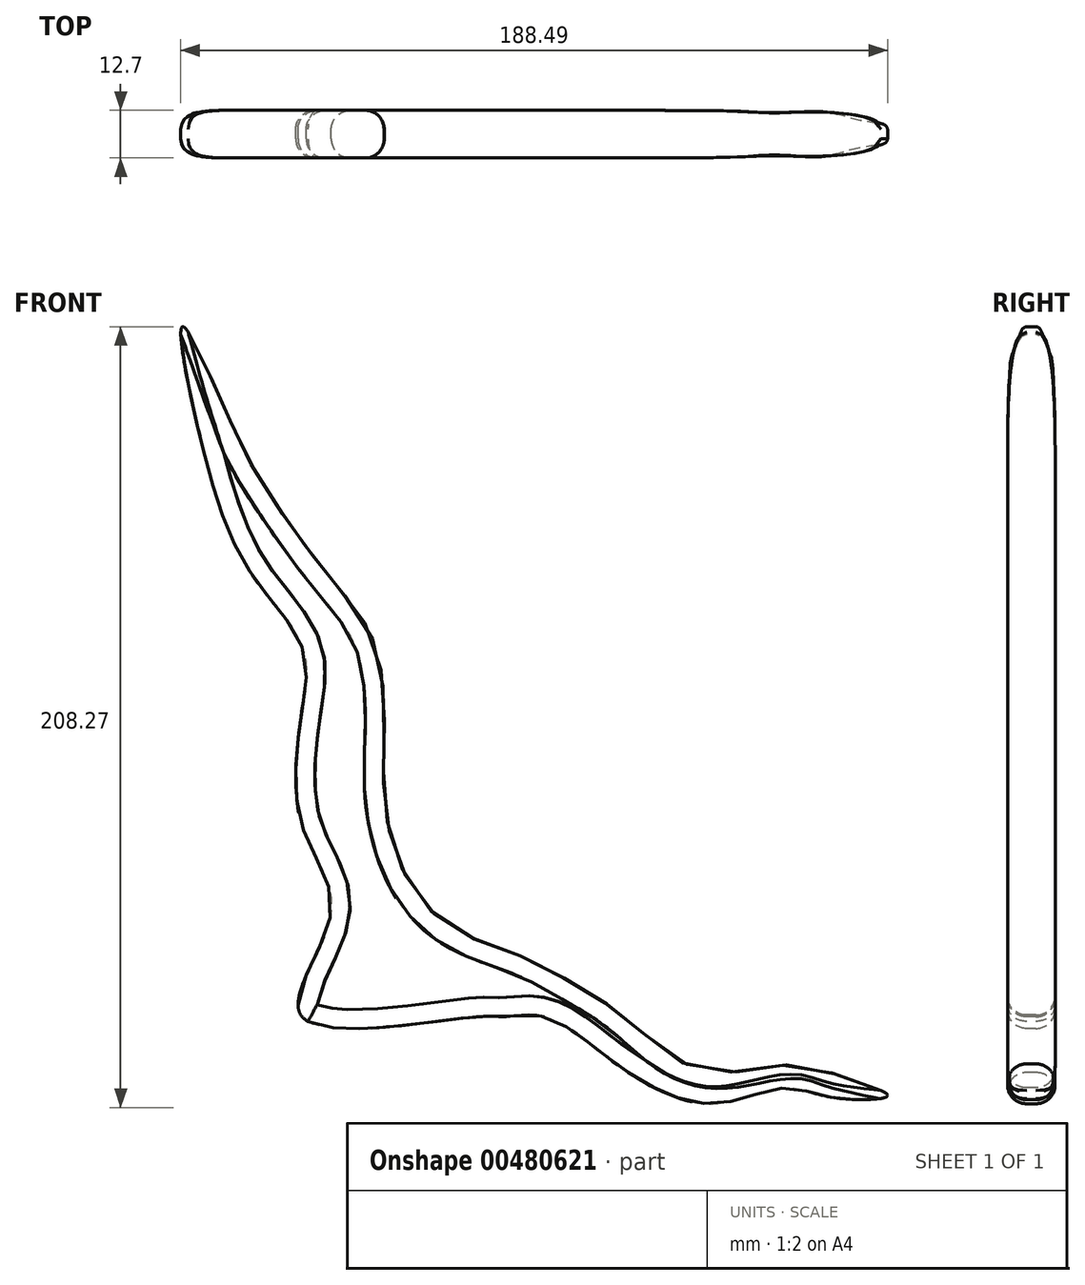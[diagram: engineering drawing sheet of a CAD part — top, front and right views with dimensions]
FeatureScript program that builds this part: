
annotation { "Feature Type Name" : "Feature", "Feature Type Description" : "" }
export const myFeature = defineFeature(function(context is Context, id is Id, definition is map)
    precondition{}
    {
        {
            var Q0;
            Q0=qCreatedBy(makeId("Front.planeOp"),FACE);
            var sketch = newSketch(context, id + "F0", { "sketchPlane" : qUnion([Q0])});
            skFitSpline(sketch, "E0", {"points": [v(0, 0) * mm, v(7.55, 27.26) * mm, v(0, 50.76) * mm, v(0, 82.18) * mm, v(0, 98.63) * mm, v(-12.44, 116.58) * mm, v(-24.84, 145.57) * mm, v(-31.91, 184.07) * mm, v(-20.9, 162.8) * mm, v(-12.51, 145.45) * mm, v(0, 126.75) * mm, v(9.05, 115.13) * mm, v(18.87, 100.64) * mm, v(21.9, 79) * mm, v(21.79, 59.56) * mm, v(25.1, 43.3) * mm, v(32.07, 30.7) * mm, v(43.54, 21.86) * mm, v(58.45, 16.1) * mm, v(71.33, 9.44) * mm, v(85.84, 0) * mm, v(100.38, -11.67) * mm, v(115.7, -14.66) * mm, v(132.9, -12.56) * mm, v(141.46, -15.02) * mm, v(156.12, -20.93) * mm, v(141.63, -21.53) * mm, v(128.68, -18.96) * mm, v(112.7, -22.9) * mm, v(97.6, -20.64) * mm, v(80.71, -10.28) * mm, v(64.4, 0) * mm, v(53.78, 0) * mm, v(46.39, 0) * mm, v(0, 0) * mm]});
            skSolve(sketch);
        }
        {
            var Q0;
            Q0 = qSketchRegion(id + "F0", true);
            extrude(context, id + "F1", {"entities" : qUnion([Q0]), "oppositeDirection" : true, "depth" : 12.7 * mm});
        }
        {
            var Q0;
            Q0=makeQuery(id+"F1.opExtrude","CAP_EDGE",EDGE,{"disambiguationData":[OSD([sQuery(id+"F0.wireOp",EDGE,"E0")])],"isStart":true});
            var Q1;
            Q1=makeQuery(id+"F1.opExtrude","CAP_EDGE",EDGE,{"disambiguationData":[OSD([sQuery(id+"F0.wireOp",EDGE,"E0")])],"isStart":false});
            fillet(context, id + "F2", {"entities" : qUnion([Q0, Q1]), "radius" : 5.08 * mm, "tangentPropagation" : true, "allowEdgeOverflow" : false});
        }
    });
